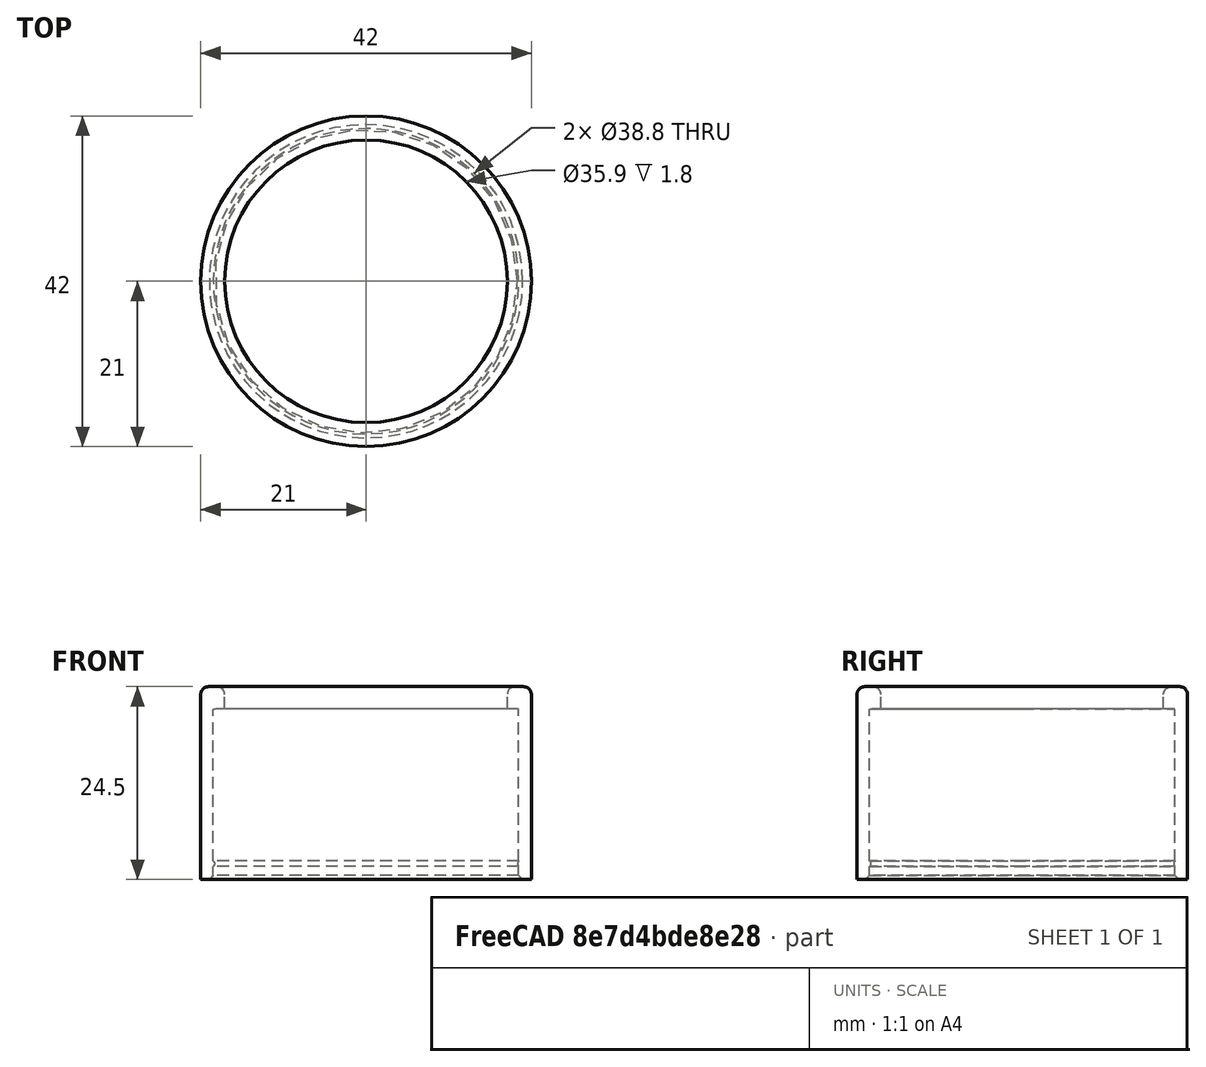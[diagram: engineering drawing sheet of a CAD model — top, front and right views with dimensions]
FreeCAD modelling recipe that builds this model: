
FCSTD DOCUMENT  (FreeCAD 0.19R24276 (Git))
Label: TapaManometroCompresor
License: All rights reserved
LicenseURL: http://en.wikipedia.org/wiki/All_rights_reserved
objects: TechDraw::DrawViewDimension×7, Part::Cylinder×3, TechDraw::DrawProjGroupItem×3, Part::Cut×2, TechDraw::DrawSVGTemplate×2, TechDraw::DrawViewPart×2, TechDraw::DrawPage×2, Part::Torus×1, Part::Offset×1, Part::MultiFuse×1, Part::Fillet×1, Part::Chamfer×1, TechDraw::DrawProjGroup×1, TechDraw::DrawViewAnnotation×1
note: 10 computed .brp shape members not serialized (recipe doc carries the construction recipe); baked Part::Feature solids carry a one-line shape summary decoded from their .brp

FEATURE [Part::Cylinder] Cylinder  label="Cilindro"
  Angle = 360
  AttacherType = Attacher::AttachEngine3D
  Height = 24.5
  Radius = 21
FEATURE [Part::Cylinder] Cylinder001  label="Cilindro001"
  Angle = 360
  AttacherType = Attacher::AttachEngine3D
  Height = 21.5
  Radius = 19.2
FEATURE [Part::Cylinder] Cylinder002  label="Cilindro002"
  Angle = 360
  AttacherType = Attacher::AttachEngine3D
  Height = 3.5
  Placement = pos=(0,0,21) rot=(0,0,1;0rad)
  Radius = 17.95
FEATURE [Part::Torus] Torus  label="Toro"
  Angle1 = -180
  Angle2 = 180
  Angle3 = 360
  AttacherType = Attacher::AttachEngine3D
  Placement = pos=(0,0,2) rot=(0,0,1;0rad)
  Radius1 = 19.75
  Radius2 = 0.5
FEATURE [Part::Offset] Offset
  Fill = false
  Intersection = false
  Join = 0
  Mode = 0
  SelfIntersection = false
  Source = -> Cylinder001
  Value = 0.2
FEATURE [Part::Cut] Cut
  Base = -> Cylinder
  Tool = -> Cylinder002
FEATURE [Part::Cut] Cut001
  Base = -> Cut
  Tool = -> Offset
FEATURE [Part::MultiFuse] Fusion
  Shapes = -> [Cut001,Torus]
FEATURE [Part::Fillet] Fillet
  Base = -> Fusion
  Edges = 2 edges r=1: [Edge1,Edge4]
FEATURE [Part::Chamfer] Chamfer
  Base = -> Fillet
  Edges = 1 edges r=0.5: [Edge6]
FEATURE [TechDraw::DrawSVGTemplate] Template
  EditableTexts = Designed_by_Name=<owner>; Drawing_number=001; FC-Date=-; FC-SC=1:1; FC-SH=1/2; FC-Title=PressureGaugeCover; Subtitle=Tapon Manometro; Weight=<100gr
  Height = 210
  Orientation = 1
  Width = 297
FEATURE [TechDraw::DrawSVGTemplate] Template001
  EditableTexts = Designed_by_Name=<owner>; Drawing_number=001; FC-Date=-; FC-SC=1:2; FC-SH=2/2; FC-Title=PressureGaugeCover; Subtitle=Tapon Manometro; Weight=<100gr
  Height = 210
  Orientation = 1
  Width = 297
FEATURE [TechDraw::DrawViewPart] View
  CoarseView = false
  Direction = (0.577,-0.577,0.577)
  Focus = 100
  HardHidden = false
  IsoCount = 0
  IsoHidden = false
  IsoVisible = false
  LockPosition = false
  Perspective = false
  Rotation = 0
  Scale = 2
  ScaleType = 0
  SeamHidden = false
  SeamVisible = true
  SmoothHidden = false
  SmoothVisible = true
  Source = -> [Chamfer]
  X = 219.178
  XDirection = (0.707,0.707,0)
  Y = 128.559
FEATURE [TechDraw::DrawProjGroupItem] ProjItem  label="Front"
  CoarseView = false
  Direction = (0,-1,0)
  Focus = 100
  HardHidden = false
  IsoCount = 0
  IsoHidden = false
  IsoVisible = false
  LockPosition = true
  Perspective = false
  Rotation = 0
  RotationVector = (1,0,0)
  ScaleType = 2
  SeamHidden = false
  SeamVisible = true
  SmoothHidden = false
  SmoothVisible = true
  Source = -> [Chamfer]
  Type = 0
  X = 0
  XDirection = (1,0,0)
  Y = 0
FEATURE [TechDraw::DrawProjGroupItem] ProjItem001  label="Right"
  CoarseView = false
  Direction = (1,-1e-16,0)
  Focus = 100
  HardHidden = false
  IsoCount = 0
  IsoHidden = false
  IsoVisible = false
  LockPosition = false
  Perspective = false
  Rotation = 0
  RotationVector = (1,0,0)
  ScaleType = 2
  SeamHidden = false
  SeamVisible = true
  SmoothHidden = false
  SmoothVisible = true
  Source = -> [Chamfer]
  Type = 2
  X = -57
  XDirection = (1e-16,1,0)
  Y = 0
FEATURE [TechDraw::DrawProjGroupItem] ProjItem002  label="Top"
  CoarseView = false
  Direction = (0,0,1)
  Focus = 100
  HardHidden = false
  IsoCount = 0
  IsoHidden = false
  IsoVisible = false
  LockPosition = false
  Perspective = false
  Rotation = 0
  RotationVector = (1,0,0)
  ScaleType = 2
  SeamHidden = false
  SeamVisible = true
  SmoothHidden = false
  SmoothVisible = true
  Source = -> [Chamfer]
  Type = 4
  X = 0
  XDirection = (1,0,0)
  Y = -57
FEATURE [TechDraw::DrawProjGroup] ProjGroup
  Anchor = -> ProjItem
  AutoDistribute = true
  LockPosition = false
  ProjectionType = 0
  Rotation = 0
  ScaleType = 2
  Source = -> [Chamfer]
  Views = -> [ProjItem,ProjItem001,ProjItem002]
  X = 114.186
  Y = 161.337
  spacingX = 15
  spacingY = 15
FEATURE [TechDraw::DrawViewDimension] Dimension
  Arbitrary = false
  ArbitraryTolerances = false
  EqualTolerance = true
  FormatSpec = %.2f
  FormatSpecOverTolerance = %+.2f
  FormatSpecUnderTolerance = %+.2f
  Inverted = false
  LockPosition = false
  MeasureType = 1
  OverTolerance = 0
  References2D = -> [ProjItem]
  Rotation = 0
  Scale = 2
  ScaleType = 0
  TheoreticalExact = false
  Type = 1
  UnderTolerance = 0
  X = -4.19881
  Y = -24.3525
FEATURE [TechDraw::DrawViewDimension] Dimension001
  Arbitrary = false
  ArbitraryTolerances = false
  EqualTolerance = true
  FormatSpec = %.2f
  FormatSpecOverTolerance = %+.2f
  FormatSpecUnderTolerance = %+.2f
  Inverted = false
  LockPosition = false
  MeasureType = 1
  OverTolerance = 0
  References2D = -> [ProjItem]
  Rotation = 0
  Scale = 2
  ScaleType = 0
  TheoreticalExact = false
  Type = 2
  UnderTolerance = 0
  X = 30.3856
  Y = -25.9399
FEATURE [TechDraw::DrawViewDimension] Dimension002
  Arbitrary = false
  ArbitraryTolerances = false
  EqualTolerance = true
  FormatSpec = ⌀%.2f
  FormatSpecOverTolerance = %+.2f
  FormatSpecUnderTolerance = %+.2f
  Inverted = false
  LockPosition = false
  MeasureType = 1
  OverTolerance = 0
  References2D = -> [ProjItem002]
  Rotation = 0
  Scale = 2
  ScaleType = 0
  TheoreticalExact = false
  Type = 5
  UnderTolerance = 0
  X = -0.939454
  Y = 2.81836
FEATURE [TechDraw::DrawPage] Page  label="Vistas"
  KeepUpdated = true
  NextBalloonIndex = 1
  ProjectionType = 0
  Scale = 2
  Template = -> Template
  Views = -> [View,ProjGroup,Dimension,Dimension001,Dimension002]
FEATURE [TechDraw::DrawViewPart] View001
  CoarseView = false
  Direction = (0.577,-0.577,0.577)
  Focus = 100
  HardHidden = false
  IsoCount = 0
  IsoHidden = false
  IsoVisible = false
  LockPosition = false
  Perspective = false
  Rotation = 0
  Scale = 2
  ScaleType = 0
  SeamHidden = false
  SeamVisible = true
  SmoothHidden = false
  SmoothVisible = true
  Source = -> [Chamfer]
  X = 142.952
  XDirection = (0.707,0.707,0)
  Y = 123.779
FEATURE [TechDraw::DrawViewDimension] Dimension003
  Arbitrary = false
  ArbitraryTolerances = false
  EqualTolerance = true
  FormatSpec = %.2f
  FormatSpecOverTolerance = %+.2f
  FormatSpecUnderTolerance = %+.2f
  Inverted = false
  LockPosition = false
  MeasureType = 1
  OverTolerance = 0
  References2D = -> [View001]
  Rotation = 0
  Scale = 2
  ScaleType = 0
  TheoreticalExact = false
  Type = 0
  UnderTolerance = 0
  X = 92.7145
  Y = -2.82424
FEATURE [TechDraw::DrawViewDimension] Dimension004
  Arbitrary = false
  ArbitraryTolerances = false
  EqualTolerance = true
  FormatSpec = %.2f
  FormatSpecOverTolerance = %+.2f
  FormatSpecUnderTolerance = %+.2f
  Inverted = false
  LockPosition = false
  MeasureType = 1
  OverTolerance = 0
  References2D = -> [View001]
  Rotation = 0
  Scale = 2
  ScaleType = 0
  TheoreticalExact = false
  Type = 0
  UnderTolerance = 0
  X = 22.5401
  Y = -22.3565
FEATURE [TechDraw::DrawViewDimension] Dimension005
  Arbitrary = false
  ArbitraryTolerances = false
  EqualTolerance = true
  FormatSpec = %.2f
  FormatSpecOverTolerance = %+.2f
  FormatSpecUnderTolerance = %+.2f
  Inverted = false
  LockPosition = false
  MeasureType = 1
  OverTolerance = 0
  References2D = -> [View001]
  Rotation = 0
  Scale = 2
  ScaleType = 0
  TheoreticalExact = false
  Type = 0
  UnderTolerance = 0
  X = -17.1219
  Y = -12.1923
FEATURE [TechDraw::DrawViewDimension] Dimension006
  Arbitrary = false
  ArbitraryTolerances = false
  EqualTolerance = true
  FormatSpec = %.2f
  FormatSpecOverTolerance = %+.2f
  FormatSpecUnderTolerance = %+.2f
  Inverted = false
  LockPosition = false
  MeasureType = 1
  OverTolerance = 0
  References2D = -> [View001]
  Rotation = 0
  Scale = 2
  ScaleType = 0
  TheoreticalExact = false
  Type = 2
  UnderTolerance = 0
  X = 60.09
  Y = -3.40311
FEATURE [TechDraw::DrawViewAnnotation] Annotation
  Font = osifont
  LineSpace = 80
  LockPosition = false
  MaxWidth = -1
  Rotation = 0
  Scale = 2
  ScaleType = 0
  Text = Aproximate measurements: | Check with 3D piece
  TextSize = 5
  TextStyle = 0
  X = 87.7208
  Y = 56.6883
FEATURE [TechDraw::DrawPage] Page001  label="Cotas"
  KeepUpdated = true
  NextBalloonIndex = 1
  ProjectionType = 0
  Scale = 2
  Template = -> Template001
  Views = -> [View001,Dimension003,Dimension004,Dimension005,Dimension006,Annotation]
